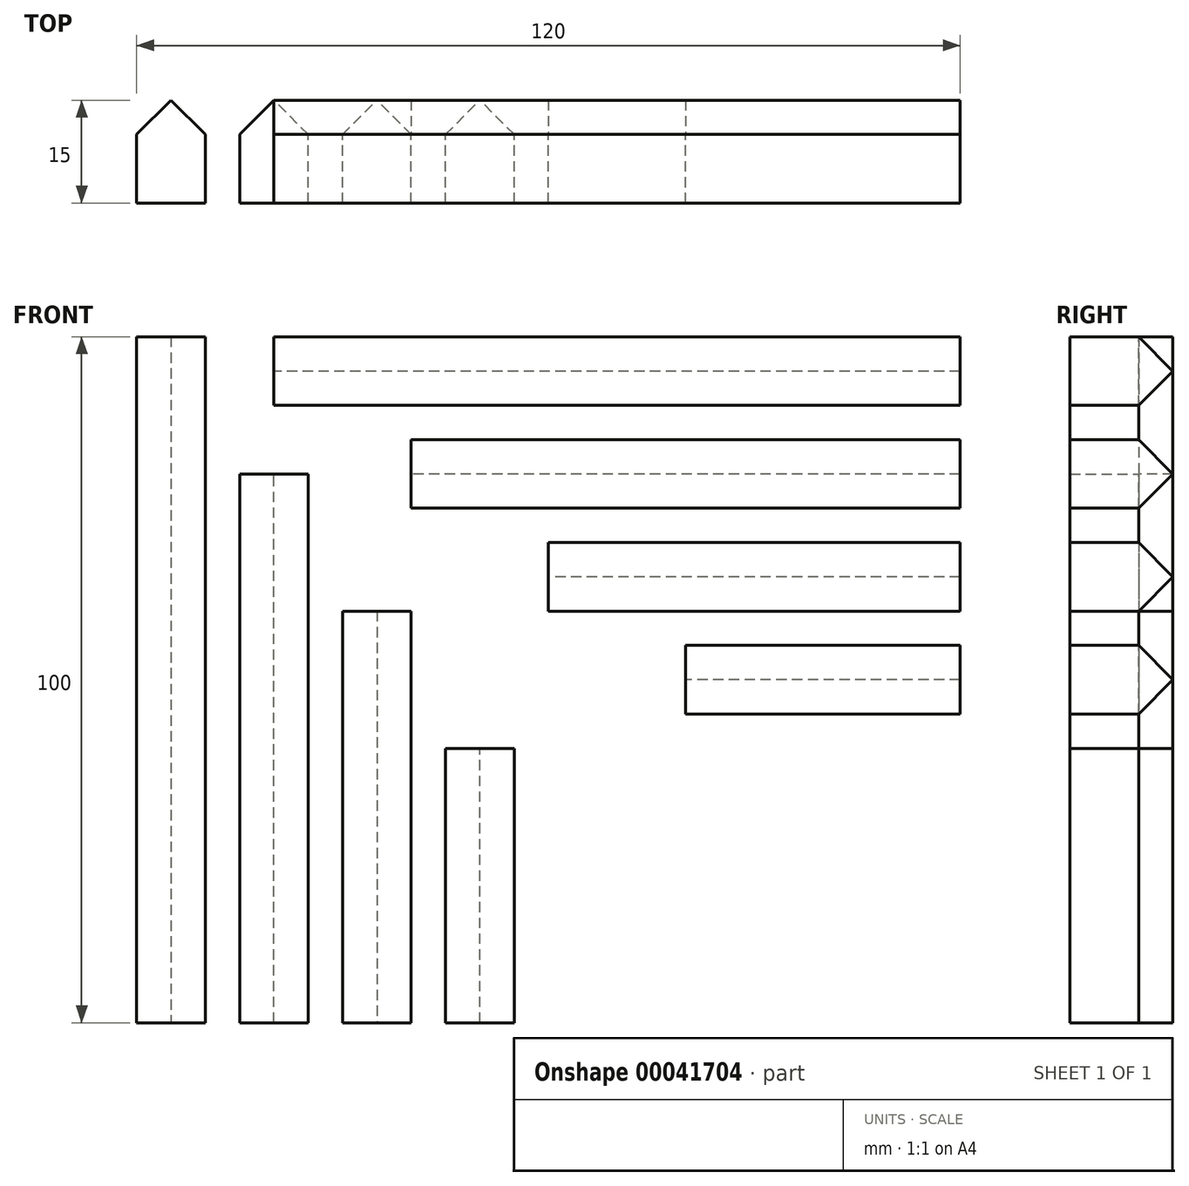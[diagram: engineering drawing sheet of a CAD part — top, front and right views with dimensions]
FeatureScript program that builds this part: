
annotation { "Feature Type Name" : "Feature", "Feature Type Description" : "" }
export const myFeature = defineFeature(function(context is Context, id is Id, definition is map)
    precondition{}
    {
        {
            var Q0;
            Q0=qCreatedBy(makeId("Front.planeOp"),FACE);
            var sketch = newSketch(context, id + "F0", { "sketchPlane" : qUnion([Q0])});
            skLineSegment(sketch, "E0.bottom", {"start": v(-81.65, 49.28) * mm, "end": v(-71.65, 49.28) * mm});
            skLineSegment(sketch, "E0.top", {"start": v(-81.65, -50.72) * mm, "end": v(-71.65, -50.72) * mm});
            skLineSegment(sketch, "E0.left", {"start": v(-81.65, 49.28) * mm, "end": v(-81.65, -50.72) * mm});
            skLineSegment(sketch, "E0.right", {"start": v(-71.65, 49.28) * mm, "end": v(-71.65, -50.72) * mm});
            skLineSegment(sketch, "E1.bottom", {"start": v(-56.65, -50.72) * mm, "end": v(-66.65, -50.72) * mm});
            skLineSegment(sketch, "E1.top", {"start": v(-56.65, 29.28) * mm, "end": v(-66.65, 29.28) * mm});
            skLineSegment(sketch, "E1.left", {"start": v(-56.65, -50.72) * mm, "end": v(-56.65, 29.28) * mm});
            skLineSegment(sketch, "E1.right", {"start": v(-66.65, -50.72) * mm, "end": v(-66.65, 29.28) * mm});
            skLineSegment(sketch, "E2.bottom", {"start": v(-51.65, 9.28) * mm, "end": v(-41.65, 9.28) * mm});
            skLineSegment(sketch, "E2.top", {"start": v(-51.65, -50.72) * mm, "end": v(-41.65, -50.72) * mm});
            skLineSegment(sketch, "E2.left", {"start": v(-51.65, 9.28) * mm, "end": v(-51.65, -50.72) * mm});
            skLineSegment(sketch, "E2.right", {"start": v(-41.65, 9.28) * mm, "end": v(-41.65, -50.72) * mm});
            skLineSegment(sketch, "E3.bottom", {"start": v(-36.65, -50.72) * mm, "end": v(-26.65, -50.72) * mm});
            skLineSegment(sketch, "E3.top", {"start": v(-36.65, -10.72) * mm, "end": v(-26.65, -10.72) * mm});
            skLineSegment(sketch, "E3.left", {"start": v(-36.65, -50.72) * mm, "end": v(-36.65, -10.72) * mm});
            skLineSegment(sketch, "E3.right", {"start": v(-26.65, -50.72) * mm, "end": v(-26.65, -10.72) * mm});
            skLineSegment(sketch, "E4.bottom", {"start": v(38.35, 49.28) * mm, "end": v(-61.65, 49.28) * mm});
            skLineSegment(sketch, "E4.top", {"start": v(38.35, 39.28) * mm, "end": v(-61.65, 39.28) * mm});
            skLineSegment(sketch, "E4.left", {"start": v(38.35, 49.28) * mm, "end": v(38.35, 39.28) * mm});
            skLineSegment(sketch, "E4.right", {"start": v(-61.65, 49.28) * mm, "end": v(-61.65, 39.28) * mm});
            skLineSegment(sketch, "E5.bottom", {"start": v(38.35, 24.28) * mm, "end": v(-41.65, 24.28) * mm});
            skLineSegment(sketch, "E5.top", {"start": v(38.35, 34.28) * mm, "end": v(-41.65, 34.28) * mm});
            skLineSegment(sketch, "E5.left", {"start": v(38.35, 24.28) * mm, "end": v(38.35, 34.28) * mm});
            skLineSegment(sketch, "E5.right", {"start": v(-41.65, 24.28) * mm, "end": v(-41.65, 34.28) * mm});
            skLineSegment(sketch, "E6.bottom", {"start": v(38.35, 19.28) * mm, "end": v(-21.65, 19.28) * mm});
            skLineSegment(sketch, "E6.top", {"start": v(38.35, 9.28) * mm, "end": v(-21.65, 9.28) * mm});
            skLineSegment(sketch, "E6.left", {"start": v(38.35, 19.28) * mm, "end": v(38.35, 9.28) * mm});
            skLineSegment(sketch, "E6.right", {"start": v(-21.65, 19.28) * mm, "end": v(-21.65, 9.28) * mm});
            skLineSegment(sketch, "E7.bottom", {"start": v(38.35, 4.28) * mm, "end": v(-1.65, 4.28) * mm});
            skLineSegment(sketch, "E7.top", {"start": v(38.35, -5.72) * mm, "end": v(-1.65, -5.72) * mm});
            skLineSegment(sketch, "E7.left", {"start": v(38.35, 4.28) * mm, "end": v(38.35, -5.72) * mm});
            skLineSegment(sketch, "E7.right", {"start": v(-1.65, 4.28) * mm, "end": v(-1.65, -5.72) * mm});
            skSolve(sketch);
        }
        {
            var Q0;
            Q0=makeQuery(id+"F0.imprint","IMPRINT",FACE,{"disambiguationData":[TD([[makeQuery(id+"F0.imprint","IMPRINT",EDGE,{"derivedFrom":sQuery(id+"F0.wireOp",EDGE,"E0.bottom")}),-1.0]])]});
            var Q1;
            Q1=makeQuery(id+"F0.imprint","IMPRINT",FACE,{"disambiguationData":[TD([[makeQuery(id+"F0.imprint","IMPRINT",EDGE,{"derivedFrom":sQuery(id+"F0.wireOp",EDGE,"E1.bottom")}),-1.0]])]});
            var Q2;
            Q2=makeQuery(id+"F0.imprint","IMPRINT",FACE,{"disambiguationData":[TD([[makeQuery(id+"F0.imprint","IMPRINT",EDGE,{"derivedFrom":sQuery(id+"F0.wireOp",EDGE,"E2.bottom")}),-1.0]])]});
            var Q3;
            Q3=makeQuery(id+"F0.imprint","IMPRINT",FACE,{"disambiguationData":[TD([[makeQuery(id+"F0.imprint","IMPRINT",EDGE,{"derivedFrom":sQuery(id+"F0.wireOp",EDGE,"E3.bottom")}),1.0]])]});
            var Q4;
            Q4=makeQuery(id+"F0.imprint","IMPRINT",FACE,{"disambiguationData":[TD([[makeQuery(id+"F0.imprint","IMPRINT",EDGE,{"derivedFrom":sQuery(id+"F0.wireOp",EDGE,"E4.bottom")}),1.0]])]});
            var Q5;
            Q5=makeQuery(id+"F0.imprint","IMPRINT",FACE,{"disambiguationData":[TD([[makeQuery(id+"F0.imprint","IMPRINT",EDGE,{"derivedFrom":sQuery(id+"F0.wireOp",EDGE,"E5.bottom")}),-1.0]])]});
            var Q6;
            Q6=makeQuery(id+"F0.imprint","IMPRINT",FACE,{"disambiguationData":[TD([[makeQuery(id+"F0.imprint","IMPRINT",EDGE,{"derivedFrom":sQuery(id+"F0.wireOp",EDGE,"E6.bottom")}),1.0]])]});
            var Q7;
            Q7=makeQuery(id+"F0.imprint","IMPRINT",FACE,{"disambiguationData":[TD([[makeQuery(id+"F0.imprint","IMPRINT",EDGE,{"derivedFrom":sQuery(id+"F0.wireOp",EDGE,"E7.bottom")}),1.0]])]});
            extrude(context, id + "F1", {"entities" : qUnion([Q0, Q1, Q2, Q3, Q4, Q5, Q6, Q7]), "depth" : 15 * mm});
        }
        {
            var Q0;
            Q0=makeQuery(id+"F1.opExtrude","CAP_EDGE",EDGE,{"disambiguationData":[OSD([sQuery(id+"F0.wireOp",EDGE,"E7.top")])],"isStart":true});
            var Q1;
            Q1=makeQuery(id+"F1.opExtrude","CAP_EDGE",EDGE,{"disambiguationData":[OSD([sQuery(id+"F0.wireOp",EDGE,"E7.bottom")])],"isStart":true});
            var Q2;
            Q2=makeQuery(id+"F1.opExtrude","CAP_EDGE",EDGE,{"disambiguationData":[OSD([sQuery(id+"F0.wireOp",EDGE,"E6.top")])],"isStart":true});
            var Q3;
            Q3=makeQuery(id+"F1.opExtrude","CAP_EDGE",EDGE,{"disambiguationData":[OSD([sQuery(id+"F0.wireOp",EDGE,"E6.bottom")])],"isStart":true});
            var Q4;
            Q4=makeQuery(id+"F1.opExtrude","CAP_EDGE",EDGE,{"disambiguationData":[OSD([sQuery(id+"F0.wireOp",EDGE,"E5.bottom")])],"isStart":true});
            var Q5;
            Q5=makeQuery(id+"F1.opExtrude","CAP_EDGE",EDGE,{"disambiguationData":[OSD([sQuery(id+"F0.wireOp",EDGE,"E5.top")])],"isStart":true});
            var Q6;
            Q6=makeQuery(id+"F1.opExtrude","CAP_EDGE",EDGE,{"disambiguationData":[OSD([sQuery(id+"F0.wireOp",EDGE,"E4.top")])],"isStart":true});
            var Q7;
            Q7=makeQuery(id+"F1.opExtrude","CAP_EDGE",EDGE,{"disambiguationData":[OSD([sQuery(id+"F0.wireOp",EDGE,"E4.bottom")])],"isStart":true});
            var Q8;
            Q8=makeQuery(id+"F1.opExtrude","CAP_EDGE",EDGE,{"disambiguationData":[OSD([sQuery(id+"F0.wireOp",EDGE,"E3.right")])],"isStart":true});
            var Q9;
            Q9=makeQuery(id+"F1.opExtrude","CAP_EDGE",EDGE,{"disambiguationData":[OSD([sQuery(id+"F0.wireOp",EDGE,"E3.left")])],"isStart":true});
            var Q10;
            Q10=makeQuery(id+"F1.opExtrude","CAP_EDGE",EDGE,{"disambiguationData":[OSD([sQuery(id+"F0.wireOp",EDGE,"E2.right")])],"isStart":true});
            var Q11;
            Q11=makeQuery(id+"F1.opExtrude","CAP_EDGE",EDGE,{"disambiguationData":[OSD([sQuery(id+"F0.wireOp",EDGE,"E2.left")])],"isStart":true});
            var Q12;
            Q12=makeQuery(id+"F1.opExtrude","CAP_EDGE",EDGE,{"disambiguationData":[OSD([sQuery(id+"F0.wireOp",EDGE,"E1.left")])],"isStart":true});
            var Q13;
            Q13=makeQuery(id+"F1.opExtrude","CAP_EDGE",EDGE,{"disambiguationData":[OSD([sQuery(id+"F0.wireOp",EDGE,"E1.right")])],"isStart":true});
            var Q14;
            Q14=makeQuery(id+"F1.opExtrude","CAP_EDGE",EDGE,{"disambiguationData":[OSD([sQuery(id+"F0.wireOp",EDGE,"E0.right")])],"isStart":true});
            var Q15;
            Q15=makeQuery(id+"F1.opExtrude","CAP_EDGE",EDGE,{"disambiguationData":[OSD([sQuery(id+"F0.wireOp",EDGE,"E0.left")])],"isStart":true});
            chamfer(context, id + "F2", {"entities" : qUnion([Q0, Q1, Q2, Q3, Q4, Q5, Q6, Q7, Q8, Q9, Q10, Q11, Q12, Q13, Q14, Q15]), "width" : 5 * mm, "tangentPropagation" : true});
        }
    });
